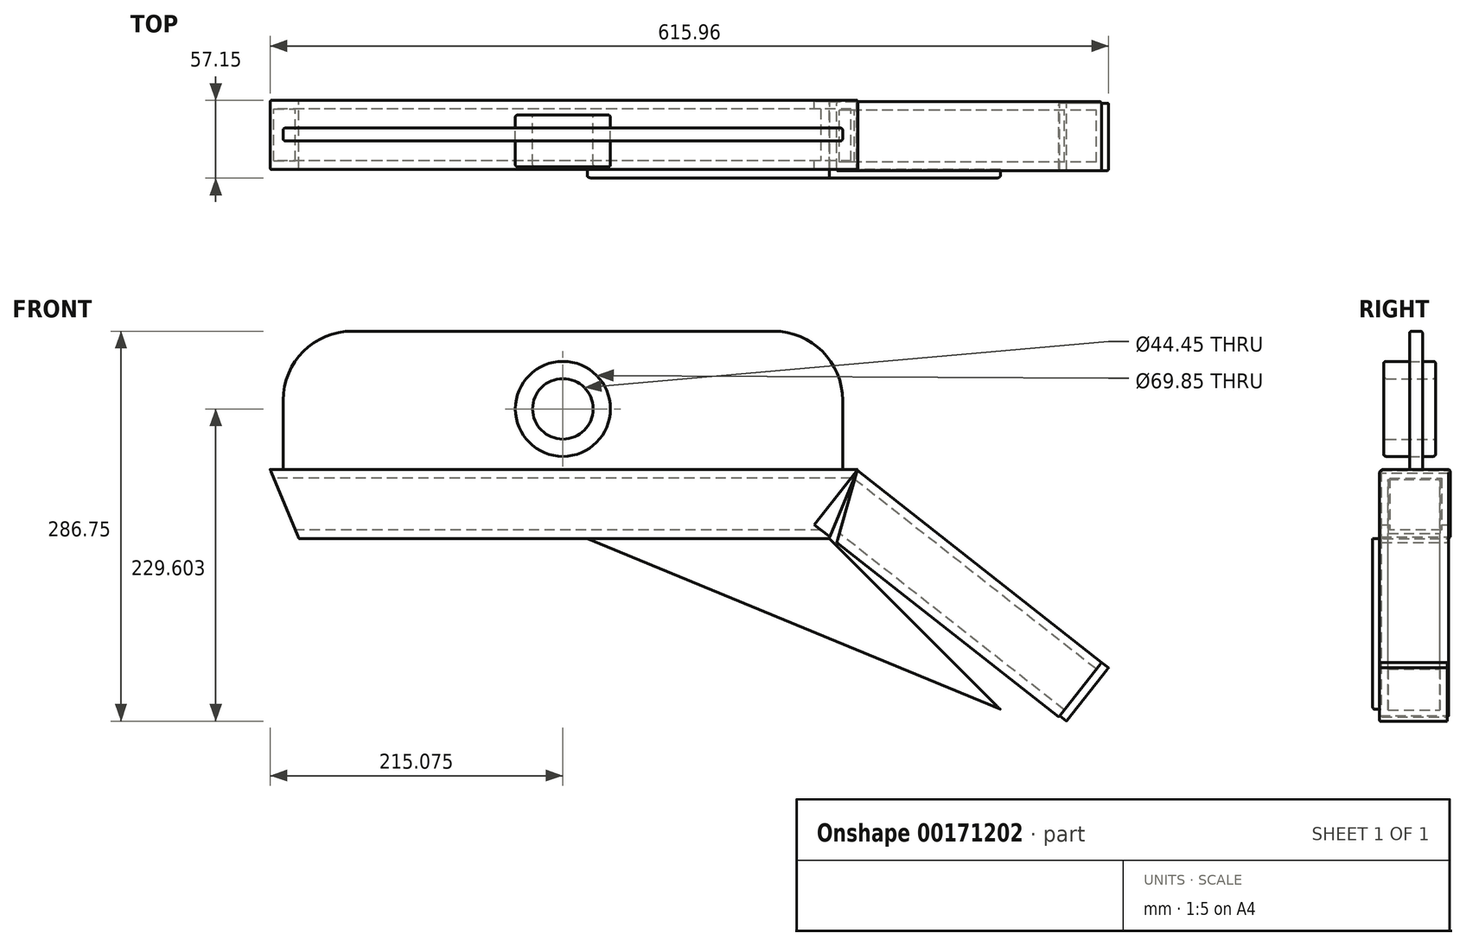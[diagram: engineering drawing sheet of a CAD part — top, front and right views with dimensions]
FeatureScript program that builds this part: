
annotation { "Feature Type Name" : "Feature", "Feature Type Description" : "" }
export const myFeature = defineFeature(function(context is Context, id is Id, definition is map)
    precondition{}
    {
        {
            var Q0;
            Q0=qCreatedBy(makeId("Right.planeOp"),FACE);
            var sketch = newSketch(context, id + "F0", { "sketchPlane" : qUnion([Q0])});
            skLineSegment(sketch, "E0.bottom", {"start": v(-43.41, 28.76) * mm, "end": v(7.39, 28.76) * mm});
            skLineSegment(sketch, "E0.top", {"start": v(-43.41, -22.04) * mm, "end": v(7.39, -22.04) * mm});
            skLineSegment(sketch, "E0.left", {"start": v(-43.41, 28.76) * mm, "end": v(-43.41, -22.04) * mm});
            skLineSegment(sketch, "E0.right", {"start": v(7.39, 28.76) * mm, "end": v(7.39, -22.04) * mm});
            skLineSegment(sketch, "E1.0", {"start": v(-37.06, 22.41) * mm, "end": v(1.04, 22.41) * mm});
            skLineSegment(sketch, "E2.0", {"start": v(1.04, 22.41) * mm, "end": v(1.04, -15.69) * mm});
            skLineSegment(sketch, "E2.1", {"start": v(-37.06, -15.69) * mm, "end": v(1.04, -15.69) * mm});
            skLineSegment(sketch, "E2.2", {"start": v(-37.06, 22.41) * mm, "end": v(-37.06, -15.69) * mm});
            skSolve(sketch);
        }
        {
            var Q0;
            Q0=makeQuery(id+"F0.imprint","IMPRINT",FACE,{"disambiguationData":[TD([[makeQuery(id+"F0.imprint","IMPRINT",EDGE,{"derivedFrom":sQuery(id+"F0.wireOp",EDGE,"E0.bottom")}),-1.0]])]});
            extrude(context, id + "F1", {"entities" : qUnion([Q0]), "endBound" : BoundingType.SYMMETRIC, "depth" : 431.8 * mm});
        }
        {
            var Q0;
            Q0=makeQuery(id+"F1.opExtrude","SWEPT_FACE",FACE,{"disambiguationData":[OSD([sQuery(id+"F0.wireOp",EDGE,"E0.right")])]});
            var sketch = newSketch(context, id + "F2", { "sketchPlane" : qUnion([Q0])});
            skLineSegment(sketch, "E3", {"start": v(-215.9, 28.76) * mm, "end": v(-194.86, -22.04) * mm});
            skLineSegment(sketch, "E4", {"start": v(215.9, 28.76) * mm, "end": v(193.15, -26.17) * mm});
            skSolve(sketch);
        }
        {
            var Q0;
            {var subQ0=sQuery(id+"F2.wireOp",EDGE,"E3");Q0=makeQuery(id+"F2.imprint","IMPRINT",FACE,{"disambiguationData":[TD([[makeQuery(id+"F2.imprint","IMPRINT",EDGE,{"derivedFrom":subQ0}),-1.0]])]});}
            var Q1;
            {var subQ1=sQuery(id+"F0.wireOp",EDGE,"E0.right");var subQ2=makeQuery(id+"F1.opExtrude","CAP_EDGE",EDGE,{"disambiguationData":[OSD([subQ1])],"isStart":true});Q1=makeQuery(id+"F2.imprint","IMPRINT",FACE,{"disambiguationData":[TD([[makeQuery(id+"F2.imprint","IMPRINT",EDGE,{"derivedFrom":subQ2}),-1.0]])]});}
            extrude(context, id + "F3", {"entities" : qUnion([Q0, Q1]), "operationType" : NewBodyOperationType.REMOVE, "endBound" : BoundingType.THROUGH_ALL, "oppositeDirection" : true, "depth" : 25.4 * mm});
        }
        {
            var Q0;
            Q0=makeQuery(id+"F1.opExtrude","SWEPT_FACE",FACE,{"disambiguationData":[OSD([sQuery(id+"F0.wireOp",EDGE,"E0.right")])]});
            var sketch = newSketch(context, id + "F4", { "sketchPlane" : qUnion([Q0])});
            skLineSegment(sketch, "E5", {"start": v(-215.9, 28.76) * mm, "end": v(-160.96, -41.18) * mm});
            skSolve(sketch);
        }
        {
            var Q0;
            Q0=qCreatedBy(makeId("Right.planeOp"),FACE);
            var Q1;
            Q1=sQuery(id+"F4.wireOp",EDGE,"E5");
            cPlane(context, id + "F5", {"entities" : qUnion([Q0, Q1]), "cplaneType" : CPlaneType.LINE_ANGLE, "offset" : 25.4 * mm, "angle" : 0 * degree, "width" : 152.4 * mm, "height" : 152.4 * mm});
        }
        {
            var Q0;
            Q0=qCreatedBy(id+"F5.planeOp",FACE);
            var sketch = newSketch(context, id + "F6", { "sketchPlane" : qUnion([Q0])});
            skLineSegment(sketch, "E6.bottom", {"start": v(44.44, 155.03) * mm, "end": v(-6.36, 155.03) * mm});
            skLineSegment(sketch, "E6.top", {"start": v(44.44, 104.23) * mm, "end": v(-6.36, 104.23) * mm});
            skLineSegment(sketch, "E6.left", {"start": v(44.44, 155.03) * mm, "end": v(44.44, 104.23) * mm});
            skLineSegment(sketch, "E6.right", {"start": v(-6.36, 155.03) * mm, "end": v(-6.36, 104.23) * mm});
            skLineSegment(sketch, "E7.0", {"start": v(38.09, 148.68) * mm, "end": v(-0.01, 148.68) * mm});
            skLineSegment(sketch, "E7.1", {"start": v(38.09, 148.68) * mm, "end": v(38.09, 110.58) * mm});
            skLineSegment(sketch, "E7.2", {"start": v(38.09, 110.58) * mm, "end": v(-0.01, 110.58) * mm});
            skLineSegment(sketch, "E7.3", {"start": v(-0.01, 148.68) * mm, "end": v(-0.01, 110.58) * mm});
            skSolve(sketch);
        }
        {
            var Q0;
            Q0=makeQuery(id+"F6.imprint","IMPRINT",FACE,{"disambiguationData":[TD([[makeQuery(id+"F6.imprint","IMPRINT",EDGE,{"derivedFrom":sQuery(id+"F6.wireOp",EDGE,"E6.bottom")}),1.0]])]});
            extrude(context, id + "F7", {"entities" : qUnion([Q0]), "oppositeDirection" : true, "depth" : 228.6 * mm});
        }
        {
            var Q0;
            Q0=makeQuery(id+"F7.opExtrude","SWEPT_FACE",FACE,{"disambiguationData":[OSD([sQuery(id+"F6.wireOp",EDGE,"E6.right")])]});
            var sketch = newSketch(context, id + "F8", { "sketchPlane" : qUnion([Q0])});
            skLineSegment(sketch, "E8", {"start": v(-215.3, 28) * mm, "end": v(-199.19, -29.51) * mm});
            skSolve(sketch);
        }
        {
            var Q0;
            {var subQ1=sQuery(id+"F6.wireOp",EDGE,"E6.right");var subQ2=makeQuery(id+"F7.opExtrude","CAP_EDGE",EDGE,{"disambiguationData":[OSD([subQ1])],"isStart":true});Q0=makeQuery(id+"F8.imprint","IMPRINT",FACE,{"disambiguationData":[TD([[makeQuery(id+"F8.imprint","IMPRINT",EDGE,{"derivedFrom":subQ2}),-1.0]])]});}
            extrude(context, id + "F9", {"entities" : qUnion([Q0]), "operationType" : NewBodyOperationType.REMOVE, "endBound" : BoundingType.THROUGH_ALL, "oppositeDirection" : true, "depth" : 25.4 * mm});
        }
        {
            var Q0;
            Q0=makeQuery(id+"F1.opExtrude","SWEPT_FACE",FACE,{"disambiguationData":[OSD([sQuery(id+"F0.wireOp",EDGE,"E0.left")])]});
            var sketch = newSketch(context, id + "F10", { "sketchPlane" : qUnion([Q0])});
            skLineSegment(sketch, "E9", {"start": v(194.86, -22.04) * mm, "end": v(17.06, -22.04) * mm});
            skLineSegment(sketch, "E10", {"start": v(194.86, -22.04) * mm, "end": v(320.58, -147.76) * mm});
            skLineSegment(sketch, "E11", {"start": v(320.58, -147.76) * mm, "end": v(17.06, -22.04) * mm});
            skSolve(sketch);
        }
        {
            var Q0;
            Q0=makeQuery(id+"F10.imprint","IMPRINT",FACE,{"disambiguationData":[TD([[makeQuery(id+"F10.imprint","IMPRINT",EDGE,{"derivedFrom":sQuery(id+"F10.wireOp",EDGE,"E9")}),1.0]])]});
            extrude(context, id + "F11", {"entities" : qUnion([Q0]), "depth" : 6.35 * mm});
        }
        {
            var Q0;
            Q0=makeQuery(id+"F1.opExtrude","SWEPT_FACE",FACE,{"disambiguationData":[OSD([sQuery(id+"F0.wireOp",EDGE,"E0.bottom")])]});
            var sketch = newSketch(context, id + "F12", { "sketchPlane" : qUnion([Q0])});
            skLineSegment(sketch, "E12.bottom", {"start": v(-206.38, -12.91) * mm, "end": v(204.72, -12.91) * mm});
            skLineSegment(sketch, "E12.top", {"start": v(-206.38, -22.44) * mm, "end": v(204.72, -22.44) * mm});
            skLineSegment(sketch, "E12.left", {"start": v(-206.38, -12.91) * mm, "end": v(-206.38, -22.44) * mm});
            skLineSegment(sketch, "E12.right", {"start": v(204.72, -12.91) * mm, "end": v(204.72, -22.44) * mm});
            skSolve(sketch);
        }
        {
            var Q0;
            Q0=makeQuery(id+"F12.imprint","IMPRINT",FACE,{"disambiguationData":[TD([[makeQuery(id+"F12.imprint","IMPRINT",EDGE,{"derivedFrom":sQuery(id+"F12.wireOp",EDGE,"E12.bottom")}),-1.0]])]});
            extrude(context, id + "F13", {"entities" : qUnion([Q0]), "depth" : 101.6 * mm});
        }
        {
            var Q0;
            Q0=makeQuery(id+"F13.opExtrude","CAP_EDGE",EDGE,{"disambiguationData":[OSD([sQuery(id+"F12.wireOp",EDGE,"E12.left")])],"isStart":false});
            var Q1;
            Q1=makeQuery(id+"F13.opExtrude","CAP_EDGE",EDGE,{"disambiguationData":[OSD([sQuery(id+"F12.wireOp",EDGE,"E12.right")])],"isStart":false});
            fillet(context, id + "F14", {"entities" : qUnion([Q0, Q1]), "radius" : 50.8 * mm, "tangentPropagation" : true, "allowEdgeOverflow" : false});
        }
        {
            var Q0;
            Q0=makeQuery(id+"F13.opExtrude","SWEPT_FACE",FACE,{"disambiguationData":[OSD([sQuery(id+"F12.wireOp",EDGE,"E12.top")])]});
            var sketch = newSketch(context, id + "F15", { "sketchPlane" : qUnion([Q0])});
            skCircle(sketch, "E13", {"center": v(-0.83, 73.21) * mm, "radius": 22.23 * mm});
            skPoint(sketch, "E13.centerSnap0", {"position": v(-0.83, 130.36) * mm});
            skSolve(sketch);
        }
        {
            var Q0;
            Q0=makeQuery(id+"F15.imprint","IMPRINT",FACE,{"disambiguationData":[TD([[makeQuery(id+"F15.imprint","IMPRINT",EDGE,{"derivedFrom":sQuery(id+"F15.wireOp",EDGE,"E13")}),1.0]])]});
            extrude(context, id + "F16", {"entities" : qUnion([Q0]), "operationType" : NewBodyOperationType.REMOVE, "oppositeDirection" : true, "depth" : 25.4 * mm});
        }
        {
            var Q0;
            Q0=makeQuery(id+"F13.opExtrude","SWEPT_FACE",FACE,{"disambiguationData":[OSD([sQuery(id+"F12.wireOp",EDGE,"E12.top")])]});
            var sketch = newSketch(context, id + "F17", { "sketchPlane" : qUnion([Q0])});
            skCircle(sketch, "E14", {"center": v(-0.83, 73.21) * mm, "radius": 34.93 * mm});
            skSolve(sketch);
        }
        {
            var Q0;
            Q0=makeQuery(id+"F17.imprint","IMPRINT",FACE,{"disambiguationData":[TD([[makeQuery(id+"F17.imprint","IMPRINT",EDGE,{"derivedFrom":sQuery(id+"F17.wireOp",EDGE,"E14")}),1.0]])]});
            extrude(context, id + "F18", {"entities" : qUnion([Q0]), "endBound" : BoundingType.SYMMETRIC, "depth" : 38.1 * mm});
        }
        {
            var Q0;
            Q0=makeQuery(id+"F18.opExtrude","SWEPT_BODY",BODY,{"disambiguationData":[OSD([sQuery(id+"F15.wireOp",EDGE,"E13"),sQuery(id+"F17.wireOp",EDGE,"E14")])]});
            var Q1;
            Q1=makeQuery(id+"F13.opExtrude","SWEPT_BODY",BODY,{"disambiguationData":[OSD([sQuery(id+"F12.wireOp",EDGE,"E12.bottom"),sQuery(id+"F12.wireOp",EDGE,"E12.top"),sQuery(id+"F12.wireOp",EDGE,"E12.left"),sQuery(id+"F12.wireOp",EDGE,"E12.right")])]});
            booleanBodies(context, id + "F19", {"operationType" : BooleanOperationType.SUBTRACTION, "tools" : qUnion([Q0]), "targets" : qUnion([Q1]), "keepTools" : true});
        }
        {
            var Q0;
            Q0=makeQuery(id+"F1.opExtrude","SWEPT_EDGE",EDGE,{"disambiguationData":[OSD([sQuery(id+"F0.wireOp",EDGE,"E0.top"),sQuery(id+"F0.wireOp",EDGE,"E0.left")])]});
            var Q1;
            Q1=makeQuery(id+"F1.opExtrude","SWEPT_EDGE",EDGE,{"disambiguationData":[OSD([sQuery(id+"F0.wireOp",EDGE,"E0.bottom"),sQuery(id+"F0.wireOp",EDGE,"E0.left")])]});
            var Q2;
            Q2=makeQuery(id+"F1.opExtrude","SWEPT_EDGE",EDGE,{"disambiguationData":[OSD([sQuery(id+"F0.wireOp",EDGE,"E0.top"),sQuery(id+"F0.wireOp",EDGE,"E0.right")])]});
            var Q3;
            Q3=makeQuery(id+"F11.opExtrude","CAP_EDGE",EDGE,{"disambiguationData":[OSD([sQuery(id+"F10.wireOp",EDGE,"E11")])],"isStart":false});
            var Q4;
            Q4=makeQuery(id+"F7.opExtrude","SWEPT_EDGE",EDGE,{"disambiguationData":[OSD([sQuery(id+"F6.wireOp",EDGE,"E6.top"),sQuery(id+"F6.wireOp",EDGE,"E6.left")])]});
            var Q5;
            Q5=makeQuery(id+"F7.opExtrude","SWEPT_EDGE",EDGE,{"disambiguationData":[OSD([sQuery(id+"F6.wireOp",EDGE,"E6.bottom"),sQuery(id+"F6.wireOp",EDGE,"E6.left")])]});
            var Q6;
            Q6=makeQuery(id+"F1.opExtrude","SWEPT_EDGE",EDGE,{"disambiguationData":[OSD([sQuery(id+"F0.wireOp",EDGE,"E0.bottom"),sQuery(id+"F0.wireOp",EDGE,"E0.right")])]});
            var Q7;
            Q7=makeQuery(id+"F7.opExtrude","SWEPT_EDGE",EDGE,{"disambiguationData":[OSD([sQuery(id+"F6.wireOp",EDGE,"E6.bottom"),sQuery(id+"F6.wireOp",EDGE,"E6.right")])]});
            var Q8;
            Q8=makeQuery(id+"F7.opExtrude","SWEPT_EDGE",EDGE,{"disambiguationData":[OSD([sQuery(id+"F6.wireOp",EDGE,"E6.top"),sQuery(id+"F6.wireOp",EDGE,"E6.right")])]});
            var Q9;
            Q9=makeQuery(id+"F13.opExtrude","SWEPT_EDGE",EDGE,{"disambiguationData":[OSD([sQuery(id+"F12.wireOp",EDGE,"E12.bottom"),sQuery(id+"F12.wireOp",EDGE,"E12.right")])]});
            var Q10;
            Q10=makeQuery(id+"F14.opFillet","BLEND_EDGE",EDGE,{"blendedFrom":[makeQuery(id+"F13.opExtrude","CAP_EDGE",EDGE,{"disambiguationData":[OSD([sQuery(id+"F12.wireOp",EDGE,"E12.right")])],"isStart":false}),makeQuery(id+"F13.opExtrude","SWEPT_FACE",FACE,{"disambiguationData":[OSD([sQuery(id+"F12.wireOp",EDGE,"E12.bottom")])]})],"blendedInto":[makeQuery(id+"F13.opExtrude","SWEPT_FACE",FACE,{"disambiguationData":[OSD([sQuery(id+"F12.wireOp",EDGE,"E12.bottom")])]})]});
            var Q11;
            Q11=makeQuery(id+"F13.opExtrude","SWEPT_EDGE",EDGE,{"disambiguationData":[OSD([sQuery(id+"F12.wireOp",EDGE,"E12.top"),sQuery(id+"F12.wireOp",EDGE,"E12.right")])]});
            fillet(context, id + "F20", {"entities" : qUnion([Q0, Q1, Q2, Q3, Q4, Q5, Q6, Q7, Q8, Q9, Q10, Q11]), "radius" : 1.65 * mm, "tangentPropagation" : true, "allowEdgeOverflow" : false});
        }
        {
            var Q0;
            Q0=makeQuery(id+"F18.opExtrude","CAP_EDGE",EDGE,{"disambiguationData":[OSD([sQuery(id+"F15.wireOp",EDGE,"E13")])],"isStart":true});
            var Q1;
            Q1=makeQuery(id+"F18.opExtrude","CAP_EDGE",EDGE,{"disambiguationData":[OSD([sQuery(id+"F17.wireOp",EDGE,"E14")])],"isStart":true});
            var Q2;
            Q2=makeQuery(id+"F18.opExtrude","CAP_EDGE",EDGE,{"disambiguationData":[OSD([sQuery(id+"F15.wireOp",EDGE,"E13")])],"isStart":false});
            var Q3;
            Q3=makeQuery(id+"F18.opExtrude","CAP_EDGE",EDGE,{"disambiguationData":[OSD([sQuery(id+"F17.wireOp",EDGE,"E14")])],"isStart":false});
            fillet(context, id + "F21", {"entities" : qUnion([Q0, Q1, Q2, Q3]), "radius" : 1.65 * mm, "tangentPropagation" : true, "allowEdgeOverflow" : false});
        }
        {
            var Q0;
            Q0=makeQuery(id+"F7.opExtrude","CAP_FACE",FACE,{"disambiguationData":[OSD([sQuery(id+"F6.wireOp",EDGE,"E6.bottom"),sQuery(id+"F6.wireOp",EDGE,"E6.top"),sQuery(id+"F6.wireOp",EDGE,"E6.left"),sQuery(id+"F6.wireOp",EDGE,"E6.right"),sQuery(id+"F6.wireOp",EDGE,"E7.0"),sQuery(id+"F6.wireOp",EDGE,"E7.1"),sQuery(id+"F6.wireOp",EDGE,"E7.2"),sQuery(id+"F6.wireOp",EDGE,"E7.3")])],"isStart":false});
            var sketch = newSketch(context, id + "F22", { "sketchPlane" : qUnion([Q0])});
            skLineSegment(sketch, "E15.bottom", {"start": v(-45.7, 155.92) * mm, "end": v(5.1, 155.92) * mm});
            skLineSegment(sketch, "E15.top", {"start": v(-45.7, 105.12) * mm, "end": v(5.1, 105.12) * mm});
            skLineSegment(sketch, "E15.left", {"start": v(-45.7, 155.92) * mm, "end": v(-45.7, 105.12) * mm});
            skLineSegment(sketch, "E15.right", {"start": v(5.1, 155.92) * mm, "end": v(5.1, 105.12) * mm});
            skSolve(sketch);
        }
        {
            var Q0;
            {var subQ5=sQuery(id+"F6.wireOp",EDGE,"E7.0");Q0=makeQuery(id+"F22.imprint","IMPRINT",FACE,{"disambiguationData":[TD([[makeQuery(id+"F22.imprint","IMPRINT",EDGE,{"derivedFrom":makeQuery(id+"F7.opExtrude","CAP_EDGE",EDGE,{"disambiguationData":[OSD([subQ5])],"isStart":false})}),1.0]])]});}
            var Q1;
            Q1=makeQuery(id+"F22.imprint","IMPRINT",FACE,{"disambiguationData":[TD([[makeQuery(id+"F22.imprint","IMPRINT",EDGE,{"derivedFrom":makeQuery(id+"F7.opExtrude","CAP_EDGE",EDGE,{"disambiguationData":[OSD([sQuery(id+"F6.wireOp",EDGE,"E7.0")])],"isStart":false})}),-1.0]])]});
            extrude(context, id + "F23", {"entities" : qUnion([Q0, Q1]), "depth" : 6.35 * mm});
        }
    });
